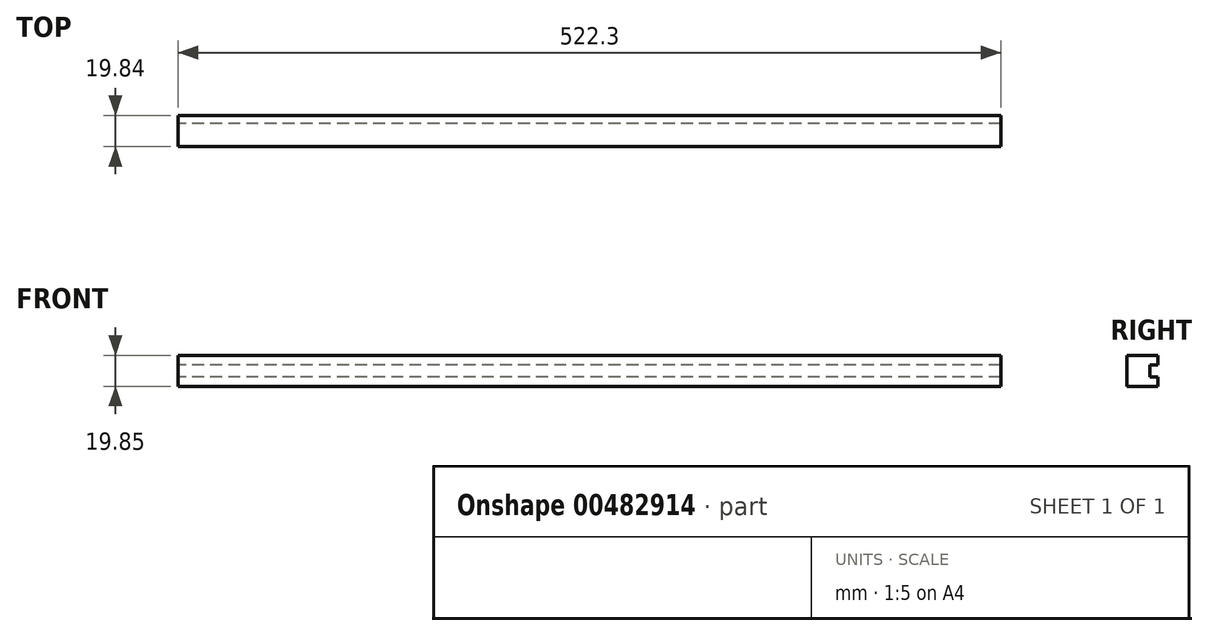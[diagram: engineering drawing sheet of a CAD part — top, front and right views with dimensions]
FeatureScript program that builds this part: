
annotation { "Feature Type Name" : "Feature", "Feature Type Description" : "" }
export const myFeature = defineFeature(function(context is Context, id is Id, definition is map)
    precondition{}
    {
        {
            var Q0;
            Q0=qCreatedBy(makeId("Right.planeOp"),FACE);
            var sketch = newSketch(context, id + "F0", { "sketchPlane" : qUnion([Q0])});
            skLineSegment(sketch, "E0.bottom", {"start": v(-38.67, 35.15) * mm, "end": v(-18.83, 35.15) * mm});
            skLineSegment(sketch, "E0.top", {"start": v(-38.67, 15.3) * mm, "end": v(-18.83, 15.3) * mm});
            skLineSegment(sketch, "E0.left", {"start": v(-38.67, 35.15) * mm, "end": v(-38.67, 15.3) * mm});
            skLineSegment(sketch, "E0.right", {"start": v(-18.83, 35.15) * mm, "end": v(-18.83, 29.04) * mm});
            skLineSegment(sketch, "E1", {"start": v(-18.83, 29.04) * mm, "end": v(-23.9, 29.04) * mm});
            skLineSegment(sketch, "E2", {"start": v(-23.9, 29.04) * mm, "end": v(-23.9, 21.42) * mm});
            skLineSegment(sketch, "E3", {"start": v(-23.9, 21.42) * mm, "end": v(-18.83, 21.42) * mm});
            skLineSegment(sketch, "E4.trimOffspring", {"start": v(-18.83, 21.42) * mm, "end": v(-18.83, 15.3) * mm});
            skSolve(sketch);
        }
        {
            var Q0;
            Q0 = qSketchRegion(id + "F0", true);
            extrude(context, id + "F1", {"entities" : qUnion([Q0]), "depth" : 522.3 * mm, "offsetDistance" : 25.4 * mm});
        }
    });
